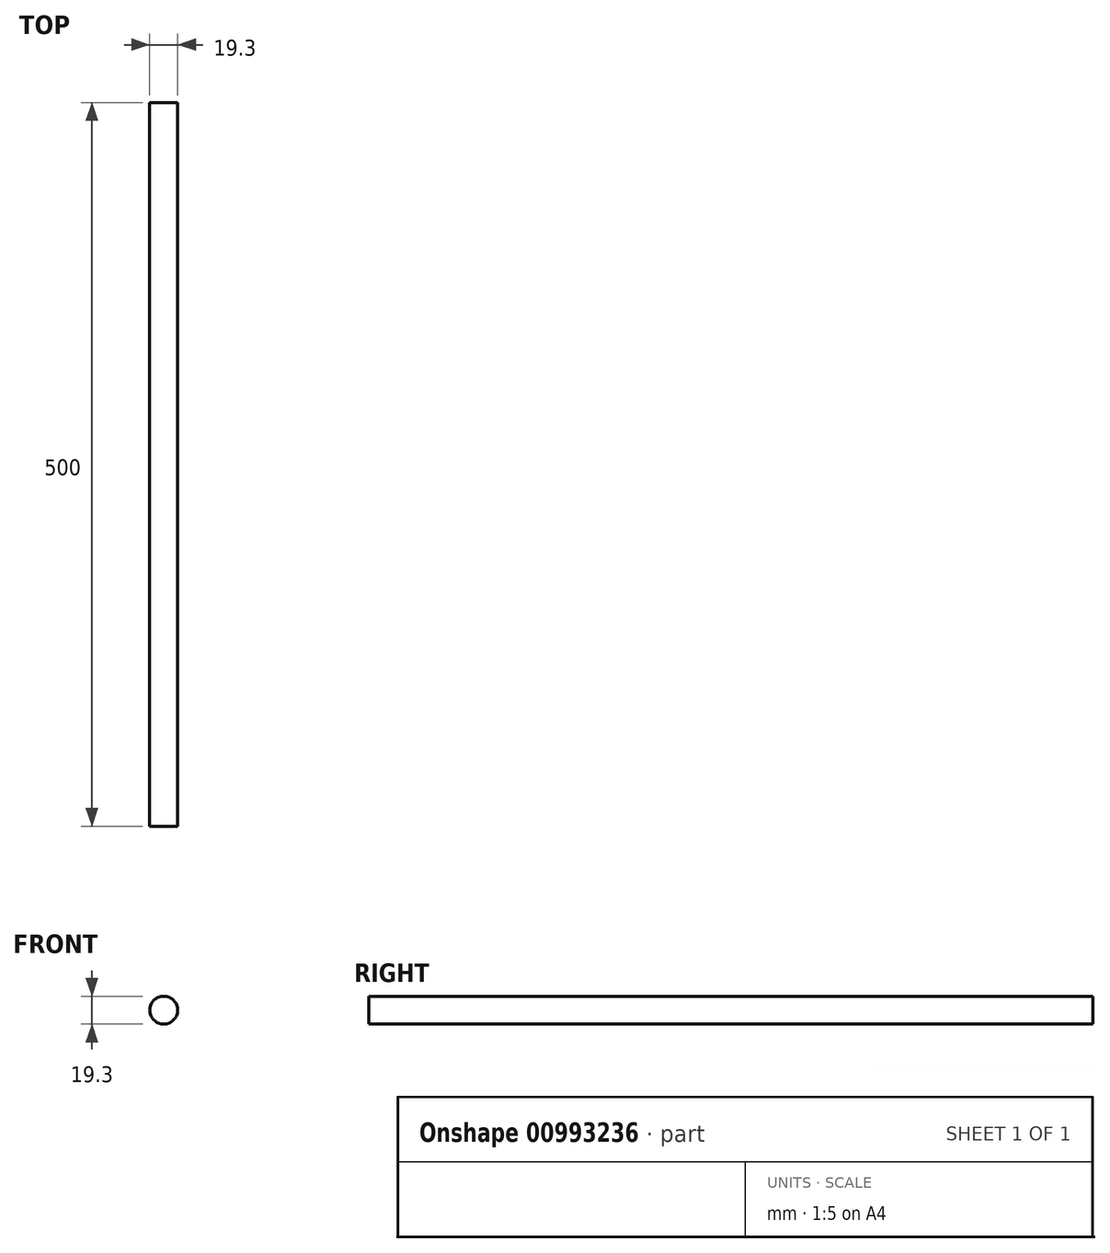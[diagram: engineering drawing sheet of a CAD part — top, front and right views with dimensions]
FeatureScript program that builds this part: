
annotation { "Feature Type Name" : "Feature", "Feature Type Description" : "" }
export const myFeature = defineFeature(function(context is Context, id is Id, definition is map)
    precondition{}
    {
        {
            var Q0;
            Q0=qCreatedBy(makeId("Front.planeOp"),FACE);
            var sketch = newSketch(context, id + "F0", { "sketchPlane" : qUnion([Q0])});
            skCircle(sketch, "E0", {"center": v(0, 0) * mm, "radius": 9.65 * mm});
            skSolve(sketch);
        }
        {
            var Q0;
            Q0 = qSketchRegion(id + "F0", true);
            extrude(context, id + "F1", {"entities" : qUnion([Q0]), "depth" : 500 * mm, "offsetDistance" : 25 * mm});
        }
    });
